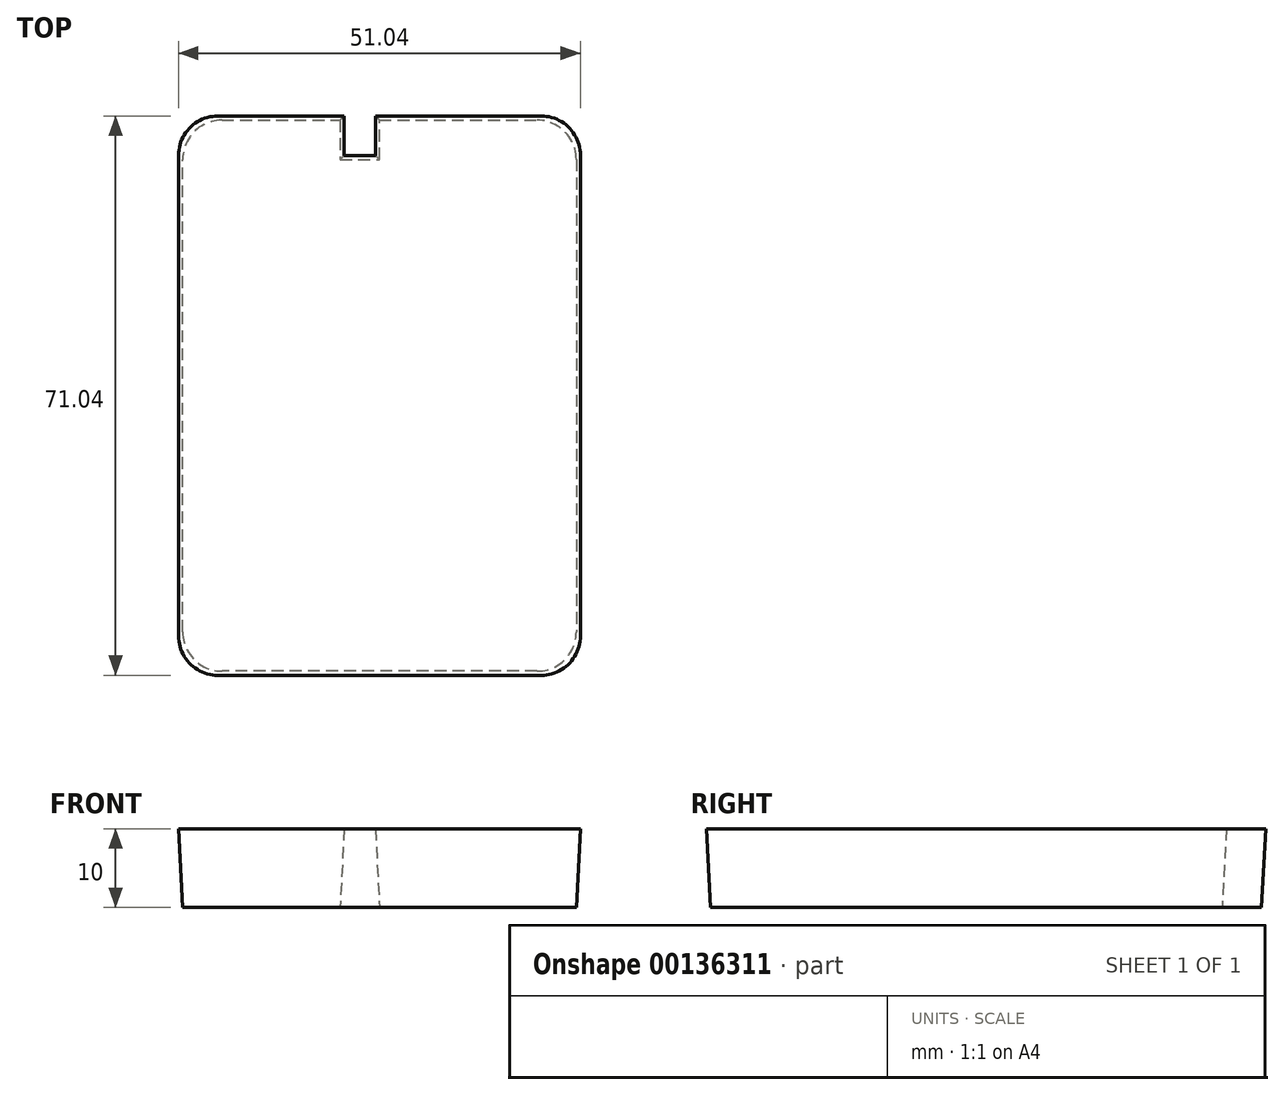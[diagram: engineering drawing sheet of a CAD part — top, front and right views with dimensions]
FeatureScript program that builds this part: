
annotation { "Feature Type Name" : "Feature", "Feature Type Description" : "" }
export const myFeature = defineFeature(function(context is Context, id is Id, definition is map)
    precondition{}
    {
        {
            var Q0;
            Q0=qCreatedBy(makeId("Top.planeOp"),FACE);
            var sketch = newSketch(context, id + "F0", { "sketchPlane" : qUnion([Q0])});
            skLineSegment(sketch, "E0.bottom", {"start": v(-25, -35) * mm, "end": v(25, -35) * mm});
            skLineSegment(sketch, "E0.top", {"start": v(-25, 35) * mm, "end": v(-5, 35) * mm});
            skLineSegment(sketch, "E0.left", {"start": v(-25, -35) * mm, "end": v(-25, 35) * mm});
            skLineSegment(sketch, "E0.right", {"start": v(25, -35) * mm, "end": v(25, 35) * mm});
            skPoint(sketch, "E0.middle", {"position": v(0, 0) * mm});
            skLineSegment(sketch, "E1", {"start": v(-5, 35) * mm, "end": v(-5, 30) * mm});
            skLineSegment(sketch, "E2", {"start": v(-5, 30) * mm, "end": v(0, 30) * mm});
            skLineSegment(sketch, "E3", {"start": v(0, 30) * mm, "end": v(0, 35) * mm});
            skLineSegment(sketch, "E4.trimOffspring", {"start": v(0, 35) * mm, "end": v(25, 35) * mm});
            skSolve(sketch);
        }
        {
            var Q0;
            Q0=makeQuery(id+"F0.imprint","IMPRINT",FACE,{"disambiguationData":[TD([[makeQuery(id+"F0.imprint","IMPRINT",EDGE,{"derivedFrom":sQuery(id+"F0.wireOp",EDGE,"E0.bottom")}),1.0]])]});
            extrude(context, id + "F1", {"entities" : qUnion([Q0]), "depth" : 10 * mm, "hasDraft" : true, "draftAngle" : 3 * degree});
        }
        {
            var Q0;
            Q0=makeQuery(id+"F1.opExtrude","SWEPT_EDGE",EDGE,{"disambiguationData":[OSD([sQuery(id+"F0.wireOp",EDGE,"E0.bottom"),sQuery(id+"F0.wireOp",EDGE,"E0.right")])]});
            var Q1;
            Q1=makeQuery(id+"F1.opExtrude","SWEPT_EDGE",EDGE,{"disambiguationData":[OSD([sQuery(id+"F0.wireOp",EDGE,"E0.right"),sQuery(id+"F0.wireOp",EDGE,"E4.trimOffspring")])]});
            var Q2;
            Q2=makeQuery(id+"F1.opExtrude","SWEPT_EDGE",EDGE,{"disambiguationData":[OSD([sQuery(id+"F0.wireOp",EDGE,"E0.bottom"),sQuery(id+"F0.wireOp",EDGE,"E0.right")])]});
            var Q3;
            Q3=makeQuery(id+"F1.opExtrude","SWEPT_EDGE",EDGE,{"disambiguationData":[OSD([sQuery(id+"F0.wireOp",EDGE,"E0.bottom"),sQuery(id+"F0.wireOp",EDGE,"E0.left")])]});
            var Q4;
            Q4=makeQuery(id+"F1.opExtrude","SWEPT_EDGE",EDGE,{"disambiguationData":[OSD([sQuery(id+"F0.wireOp",EDGE,"E0.top"),sQuery(id+"F0.wireOp",EDGE,"E0.left")])]});
            fillet(context, id + "F2", {"entities" : qUnion([Q0, Q1, Q2, Q3, Q4]), "radius" : 5 * mm, "tangentPropagation" : true, "allowEdgeOverflow" : false});
        }
    });
